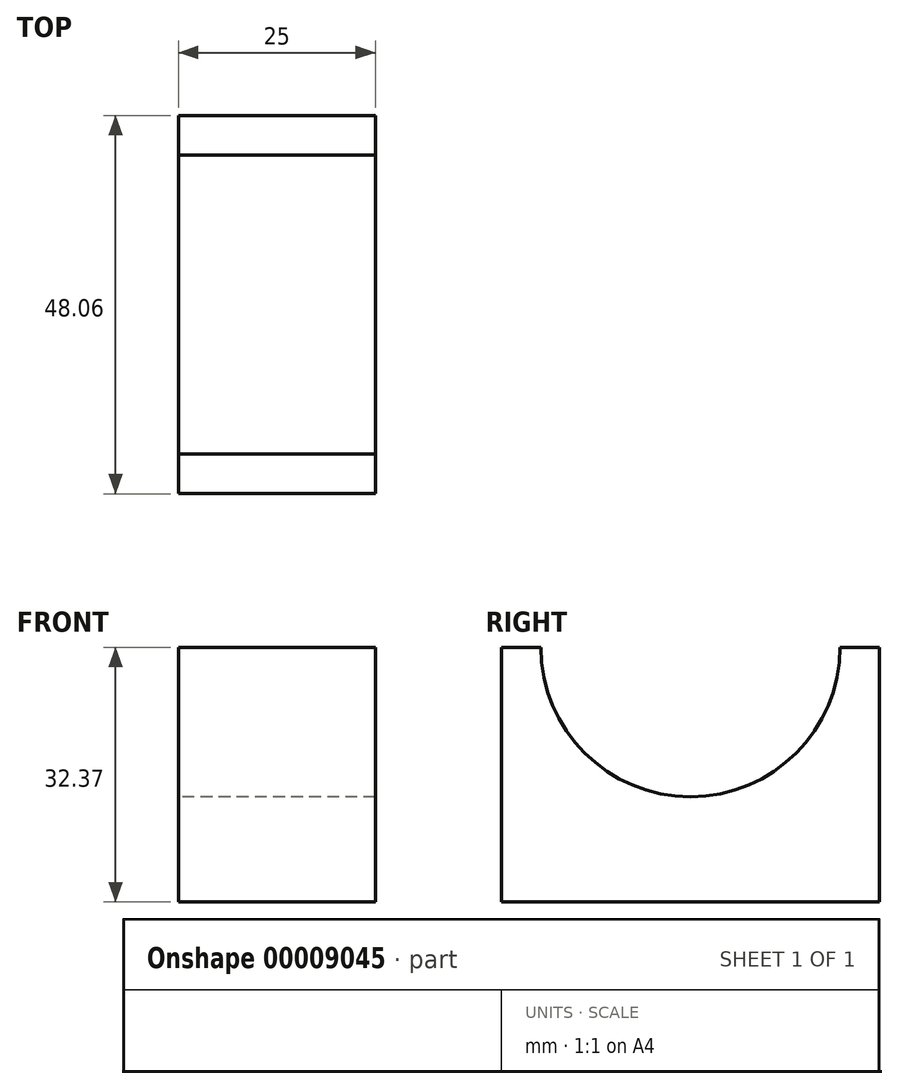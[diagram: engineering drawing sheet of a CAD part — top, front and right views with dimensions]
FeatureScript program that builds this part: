
annotation { "Feature Type Name" : "Feature", "Feature Type Description" : "" }
export const myFeature = defineFeature(function(context is Context, id is Id, definition is map)
    precondition{}
    {
        {
            var Q0;
            Q0=qCreatedBy(makeId("Right.planeOp"),FACE);
            var sketch = newSketch(context, id + "F0", { "sketchPlane" : qUnion([Q0])});
            skLineSegment(sketch, "E0", {"start": v(19.79, 0) * mm, "end": v(19.79, -32.37) * mm, "construction": true});
            skLineSegment(sketch, "E1", {"start": v(19.79, 0) * mm, "end": v(19.79, -32.37) * mm});
            skLineSegment(sketch, "E2", {"start": v(19.79, -32.37) * mm, "end": v(-18.37, -32.33) * mm});
            skLineSegment(sketch, "E3", {"start": v(-18.37, -32.33) * mm, "end": v(-18.21, 0) * mm});
            skArc(sketch, "E4", {"start": v(-18.21, 0) * mm, "mid": v(0.79, -19) * mm, "end": v(19.79, 0) * mm});
            skLineSegment(sketch, "E5.bottom", {"start": v(-18.21, 0) * mm, "end": v(-23.24, 0) * mm});
            skLineSegment(sketch, "E5.top", {"start": v(-18.21, -32.33) * mm, "end": v(-23.24, -32.33) * mm});
            skLineSegment(sketch, "E5.left", {"start": v(-18.21, 0) * mm, "end": v(-18.21, -32.33) * mm});
            skLineSegment(sketch, "E5.right", {"start": v(-23.24, 0) * mm, "end": v(-23.24, -32.33) * mm});
            skLineSegment(sketch, "E6.bottom", {"start": v(19.79, -32.37) * mm, "end": v(24.82, -32.37) * mm});
            skLineSegment(sketch, "E6.top", {"start": v(19.79, 0) * mm, "end": v(24.82, 0) * mm});
            skLineSegment(sketch, "E6.left", {"start": v(19.79, -32.37) * mm, "end": v(19.79, 0) * mm});
            skLineSegment(sketch, "E6.right", {"start": v(24.82, -32.37) * mm, "end": v(24.82, 0) * mm});
            skSolve(sketch);
        }
        {
            var Q0;
            Q0 = qSketchRegion(id + "F0", true);
            extrude(context, id + "F1", {"entities" : qUnion([Q0]), "depth" : 25 * mm});
        }
    });
